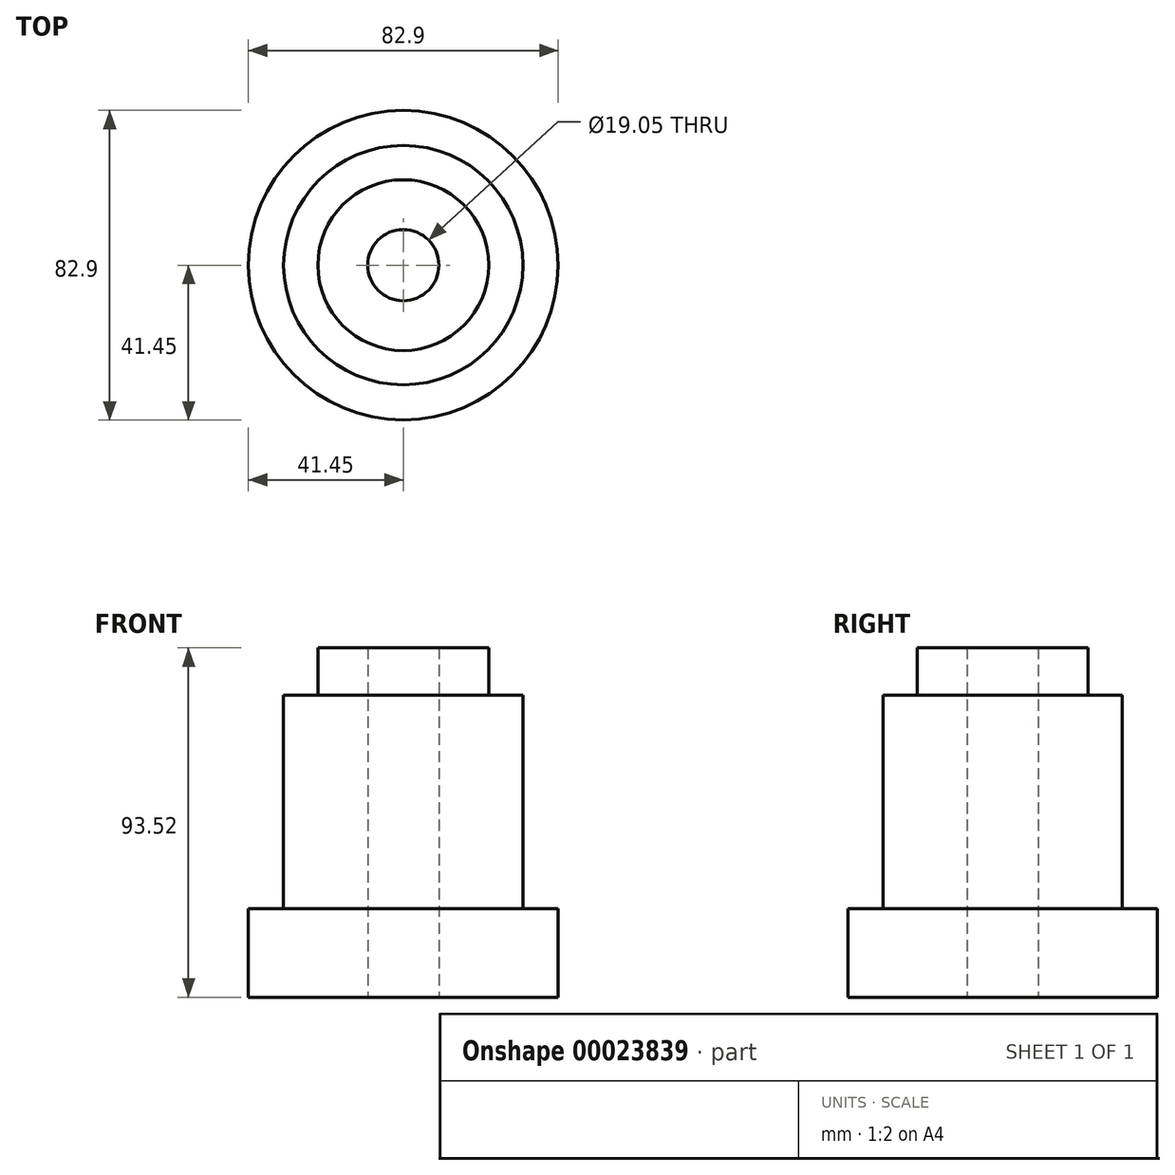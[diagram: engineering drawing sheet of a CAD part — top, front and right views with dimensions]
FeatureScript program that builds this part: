
annotation { "Feature Type Name" : "Feature", "Feature Type Description" : "" }
export const myFeature = defineFeature(function(context is Context, id is Id, definition is map)
    precondition{}
    {
        {
            var Q0;
            Q0=qCreatedBy(makeId("Front.planeOp"),FACE);
            var sketch = newSketch(context, id + "F0", { "sketchPlane" : qUnion([Q0])});
            skLineSegment(sketch, "E0", {"start": v(0, 0) * mm, "end": v(0, 116.18) * mm, "construction": true});
            skLineSegment(sketch, "E1.bottom", {"start": v(-9.53, 23.67) * mm, "end": v(-32.03, 23.67) * mm});
            skLineSegment(sketch, "E1.top", {"start": v(-9.53, 80.82) * mm, "end": v(-32.03, 80.82) * mm});
            skLineSegment(sketch, "E1.left", {"start": v(-9.53, 23.67) * mm, "end": v(-9.53, 80.82) * mm});
            skLineSegment(sketch, "E1.right", {"start": v(-32.03, 23.67) * mm, "end": v(-32.03, 80.82) * mm});
            skLineSegment(sketch, "E2.bottom", {"start": v(-9.53, 80.82) * mm, "end": v(-22.86, 80.82) * mm});
            skLineSegment(sketch, "E2.top", {"start": v(-9.53, 93.52) * mm, "end": v(-22.86, 93.52) * mm});
            skLineSegment(sketch, "E2.left", {"start": v(-9.53, 80.82) * mm, "end": v(-9.53, 93.52) * mm});
            skLineSegment(sketch, "E2.right", {"start": v(-22.86, 80.82) * mm, "end": v(-22.86, 93.52) * mm});
            skLineSegment(sketch, "E3.bottom", {"start": v(-9.53, 23.67) * mm, "end": v(-41.45, 23.67) * mm});
            skLineSegment(sketch, "E3.top", {"start": v(-9.53, 0) * mm, "end": v(-41.45, 0) * mm});
            skLineSegment(sketch, "E3.left", {"start": v(-9.53, 23.67) * mm, "end": v(-9.53, 0) * mm});
            skLineSegment(sketch, "E3.right", {"start": v(-41.45, 23.67) * mm, "end": v(-41.45, 0) * mm});
            skSolve(sketch);
        }
        {
            var Q0;
            Q0 = qSketchRegion(id + "F0", true);
            var Q1;
            Q1=sQuery(id+"F0.wireOp",EDGE,"E0");
            revolve(context, id + "F1", {"entities" : qUnion([Q0]), "axis" : qUnion([Q1]), "revolveType" : RevolveType.FULL});
        }
    });
